FREECAD ASSEMBLY — COMPONENT RECIPES ("cargotrailer_assembly")

This assembly document has 35 components, labeled P0..P34 below (a component is one placed body or linked part). 13 of them carry a construction recipe — the FreeCAD feature program that regenerates the part from scratch, quoted from this document or its linked companion documents; the rest are supplied as boundary geometry only. No exploded tour is included for this assembly.
COMPONENT P0 — recipe-attached ("framefront", a linked part whose construction recipe lives in a companion FreeCAD document of the same project; that document's serialized recipe follows).
Construction recipe (the companion document, serialized — sketch geometry with constraints, then the solid features built on it; lengths are millimeters unless a unit is written):

FCSTD DOCUMENT  (FreeCAD 0.20R29177 (Git))
Label: rightcornersupport
License: All rights reserved
LicenseURL: http://en.wikipedia.org/wiki/All_rights_reserved
objects: Sketcher::SketchObject×4, PartDesign::Pad×2, PartDesign::Pocket×2, PartDesign::LinearPattern×2, PartDesign::MultiTransform×1, PartDesign::Body×1
note: 16 computed .brp shape members not serialized (recipe doc carries the construction recipe); baked Part::Feature solids carry a one-line shape summary decoded from their .brp

FEATURE [Sketcher::SketchObject] Sketch
  FullyConstrained = true
  MapMode = 5
  Placement = pos=(0,0,0) rot=(1,0,0;1.5708rad)
  Support = -> [XZ_Plane]
  sketch-geometry (4):
    g0: LineSegment StartX=0 StartY=0 StartZ=0 EndX=45 EndY=0 EndZ=0
    g1: LineSegment StartX=45 StartY=0 StartZ=0 EndX=45 EndY=42 EndZ=0
    g2: LineSegment StartX=45 StartY=42 StartZ=0 EndX=0 EndY=42 EndZ=0
    g3: LineSegment StartX=0 StartY=42 StartZ=0 EndX=0 EndY=0 EndZ=0
  constraints (11):
    c: Coincident(g0,g1)
    c: Coincident(g1,g2)
    c: Coincident(g2,g3)
    c: Coincident(g3,g0)
    c: Horizontal(g0)
    c: Horizontal(g2)
    c: Vertical(g1)
    c: Vertical(g3)
    c: Coincident(g0,g-1)
    c: DistanceY(g1,g1) = 42
    c: DistanceX(g0,g0) = 45
FEATURE [PartDesign::Pad] Pad
  Direction = (1,1,1)
  Length = 1.6
  Length2 = 100
  Placement = pos=(0,0,0) rot=(1,0,0;1.5708rad)
  Profile = -> Sketch
  Type = 0
FEATURE [Sketcher::SketchObject] Sketch001
  ExternalGeometry = -> [Pad]
  FullyConstrained = true
  MapMode = 5
  Placement = pos=(0,0,0) rot=(-1,0,0;1.5708rad)
  Support = -> [Pad]
  sketch-geometry (4):
    g0: LineSegment StartX=0 StartY=0 StartZ=0 EndX=45 EndY=0 EndZ=0
    g1: LineSegment StartX=45 StartY=0 StartZ=0 EndX=45 EndY=-1.6 EndZ=0
    g2: LineSegment StartX=45 StartY=-1.6 StartZ=0 EndX=0 EndY=-1.6 EndZ=0
    g3: LineSegment StartX=0 StartY=-1.6 StartZ=0 EndX=0 EndY=0 EndZ=0
  constraints (11):
    c: Coincident(g0,g1)
    c: Coincident(g1,g2)
    c: Coincident(g2,g3)
    c: Coincident(g3,g0)
    c: Horizontal(g0)
    c: Horizontal(g2)
    c: Vertical(g1)
    c: Vertical(g3)
    c: Coincident(g0,g-1)
    c: PointOnObject(g1,g-3)
    c: DistanceY(g1,g1) = 1.6
FEATURE [PartDesign::Pad] Pad001
  BaseFeature = -> Pad
  Direction = (1,1,1)
  Length = 31
  Length2 = 100
  Placement = pos=(0,0,0) rot=(1,0,0;1.5708rad)
  Profile = -> Sketch001
  Type = 0
FEATURE [Sketcher::SketchObject] Sketch002
  ExternalGeometry = -> [Pad001]
  FullyConstrained = true
  MapMode = 5
  Placement = pos=(0,-1.6,7e-16) rot=(1,0,0;1.5708rad)
  Support = -> [Pad001]
  sketch-geometry (1):
    g0: Circle CenterX=22.5 CenterY=23.75 CenterZ=0 NormalX=0 NormalY=0 NormalZ=1 AngleXU=0 Radius=7.25
  constraints (3):
    c: Radius(g0) = 7.25
    c: DistanceY(g-1,g0) = 23.75
    c: DistanceX(g-1,g0) = 22.5
FEATURE [PartDesign::Pocket] Pocket
  BaseFeature = -> Pad001
  Direction = (1,1,1)
  Length = 5
  Length2 = 100
  Placement = pos=(0,0,0) rot=(1,0,0;1.5708rad)
  Profile = -> Sketch002
  Type = 1
FEATURE [Sketcher::SketchObject] Sketch003
  FullyConstrained = true
  MapMode = 5
  Placement = pos=(0,1.9e-15,1.6) rot=(0,0,1;3.14159rad)
  Support = -> [Pocket]
  expr: Constraints[1] = 3.3 + 3
  expr: Constraints[2] = 8.9 + 3
  sketch-geometry (1):
    g0: Circle CenterX=-6.3 CenterY=-11.9 CenterZ=0 NormalX=0 NormalY=0 NormalZ=1 AngleXU=0 Radius=3
  constraints (3):
    c: Radius(g0) = 3
    c: DistanceX(g0,g-1) = 6.3
    c: DistanceY(g0,g-1) = 11.9
FEATURE [PartDesign::Pocket] Pocket001
  BaseFeature = -> Pocket
  Direction = (1,1,1)
  Length = 5
  Length2 = 100
  Placement = pos=(0,0,0) rot=(1,0,0;1.5708rad)
  Profile = -> Sketch003
  Type = 1
FEATURE [PartDesign::LinearPattern] LinearPattern
  Direction = -> Y_Axis
  Length = 9.6
  Occurrences = 2
  Placement = pos=(0,0,0) rot=(1,0,0;1.5708rad)
  expr: Length = 3.6 + 6
FEATURE [PartDesign::LinearPattern] LinearPattern001
  Direction = -> X_Axis
  Length = 31
  Occurrences = 2
  Placement = pos=(0,0,0) rot=(1,0,0;1.5708rad)
  expr: Length = 25 + 6
FEATURE [PartDesign::MultiTransform] MultiTransform
  BaseFeature = -> Pocket001
  Originals = -> [Pocket001]
  Placement = pos=(0,0,0) rot=(1,0,0;1.5708rad)
  Transformations = -> [LinearPattern,LinearPattern001]
FEATURE [PartDesign::Body] Body  label="rightcornersupport"
  Group = -> [Sketch,Pad,Sketch001,Pad001,Sketch002,Pocket,Sketch003,Pocket001,MultiTransform,LinearPattern,LinearPattern001]
  Origin = -> Origin
  Tip = -> MultiTransform
COMPONENT P1 — same part as P0; its construction recipe is shown at P0.
COMPONENT P2 — same part as P0; its construction recipe is shown at P0.
COMPONENT P3 — same part as P0; its construction recipe is shown at P0.
COMPONENT P4 — geometry summary ("framecorner003"; no construction recipe available for this part):
  bounding box: 160.0 x 30.0 x 30.0 mm
  tessellated surface: 12 triangles
  volume: 144000 mm^3 (100% of its bounding box)
  symmetry: 4-fold rotationally symmetric about the z axis; mirror-symmetric across its x mid-plane, y mid-plane, z mid-plane
COMPONENT P5 — geometry summary ("framesideright002"; no construction recipe available for this part):
  bounding box: 460.0 x 30.0 x 30.0 mm
  tessellated surface: 12 triangles
  volume: 414000 mm^3 (100% of its bounding box)
  symmetry: 2-fold rotationally symmetric about the x axis; 2-fold rotationally symmetric about the y axis; 2-fold rotationally symmetric about the z axis; mirror-symmetric across its y mid-plane
COMPONENT P6 — geometry summary ("framerear002"; no construction recipe available for this part):
  bounding box: 300.0 x 30.0 x 30.0 mm
  tessellated surface: 12 triangles
  volume: 270000 mm^3 (100% of its bounding box)
  symmetry: 4-fold rotationally symmetric about the x axis; 2-fold rotationally symmetric about the z axis; mirror-symmetric across its x mid-plane, y mid-plane, z mid-plane
COMPONENT P7 — geometry summary ("framecorner007"; no construction recipe available for this part):
  bounding box: 160.0 x 30.0 x 30.0 mm
  tessellated surface: 12 triangles
  volume: 144000 mm^3 (100% of its bounding box)
  symmetry: 4-fold rotationally symmetric about the z axis; mirror-symmetric across its x mid-plane, y mid-plane, z mid-plane
COMPONENT P8 — same part as P0; its construction recipe is shown at P0.
COMPONENT P9 — geometry summary ("rightcornersupport003"; no construction recipe available for this part):
  bounding box: 45.0 x 42.0 x 32.6 mm
  tessellated surface: 1,460 triangles
  volume: 4811 mm^3 (8% of its bounding box)
COMPONENT P10 — geometry summary ("reflectorfront001"; no construction recipe available for this part):
  bounding box: 60.0 x 60.0 x 27.0 mm
  tessellated surface: 1,180 triangles
  volume: 24653 mm^3 (25% of its bounding box)
  symmetry: revolution-symmetric about the y axis through its bounding-box center
COMPONENT P11 — geometry summary ("reflectorrear001"; no construction recipe available for this part):
  bounding box: 60.0 x 60.0 x 27.0 mm
  tessellated surface: 1,180 triangles
  volume: 24653 mm^3 (25% of its bounding box)
  symmetry: revolution-symmetric about the y axis through its bounding-box center
COMPONENT P12 — same part as P0; its construction recipe is shown at P0.
COMPONENT P13 — geometry summary ("rightcornersupport005"; no construction recipe available for this part):
  bounding box: 45.0 x 42.0 x 32.6 mm
  tessellated surface: 1,460 triangles
  volume: 4811 mm^3 (8% of its bounding box)
COMPONENT P14 — geometry summary ("wheel200mm001"; no construction recipe available for this part):
  bounding box: 200.0 x 199.9 x 32.0 mm
  tessellated surface: 19,400 triangles
  volume: 579336 mm^3 (45% of its bounding box)
  symmetry: mirror-symmetric across its x mid-plane
COMPONENT P15 — geometry summary ("Corner003"; no construction recipe available for this part):
  bounding box: 100.0 x 100.0 x 1.5 mm
  tessellated surface: 1,000 triangles
  volume: 4015 mm^3 (27% of its bounding box)
  symmetry: mirror-symmetric across its y mid-plane
COMPONENT P16 — geometry summary ("Do It Garden Raccord 160x065"; no construction recipe available for this part):
  bounding box: 160.0 x 60.0 x 2.0 mm
  tessellated surface: 4,716 triangles
  volume: 18258 mm^3 (95% of its bounding box)
  symmetry: mirror-symmetric across its z mid-plane
COMPONENT P17 — geometry summary ("Do it Garden Equerre 100x100x017"; no construction recipe available for this part):
  bounding box: 100.0 x 100.0 x 1.5 mm
  tessellated surface: 1,000 triangles
  volume: 4015 mm^3 (27% of its bounding box)
  symmetry: mirror-symmetric across its y mid-plane
COMPONENT P18 — same part as P0; its construction recipe is shown at P0.
COMPONENT P19 — geometry summary ("framecorner009"; no construction recipe available for this part):
  bounding box: 160.0 x 30.0 x 30.0 mm
  tessellated surface: 12 triangles
  volume: 144000 mm^3 (100% of its bounding box)
  symmetry: 4-fold rotationally symmetric about the z axis; mirror-symmetric across its x mid-plane, y mid-plane, z mid-plane
COMPONENT P20 — geometry summary ("Do it Garden Plaque de renfort 48x026"; no construction recipe available for this part):
  bounding box: 48.0 x 15.0 x 2.0 mm
  tessellated surface: 796 triangles
  volume: 1283 mm^3 (89% of its bounding box)
  symmetry: 2-fold rotationally symmetric about the x axis; 2-fold rotationally symmetric about the y axis; 2-fold rotationally symmetric about the z axis; mirror-symmetric across its y mid-plane
COMPONENT P21 — geometry summary ("Do it Garden Equerre 70x36x017"; no construction recipe available for this part):
  bounding box: 70.0 x 52.0 x 1.5 mm
  tessellated surface: 1,212 triangles
  volume: 2367 mm^3 (43% of its bounding box)
COMPONENT P22 — geometry summary ("Do it Garden Equerre 70x36x019"; no construction recipe available for this part):
  bounding box: 70.0 x 52.0 x 1.5 mm
  tessellated surface: 1,212 triangles
  volume: 2367 mm^3 (43% of its bounding box)
COMPONENT P23 — geometry summary ("Do it Garden Equerre 30x30x031"; no construction recipe available for this part):
  bounding box: 31.5 x 31.5 x 30.0 mm
  tessellated surface: 808 triangles
  volume: 2650 mm^3 (9% of its bounding box)
COMPONENT P24 — geometry summary ("Do it Garden Equerre 30x30x033"; no construction recipe available for this part):
  bounding box: 31.5 x 31.5 x 30.0 mm
  tessellated surface: 808 triangles
  volume: 2650 mm^3 (9% of its bounding box)
COMPONENT P25 — same part as P0; its construction recipe is shown at P0.
COMPONENT P26 — same part as P0; its construction recipe is shown at P0.
COMPONENT P27 — same part as P0; its construction recipe is shown at P0.
COMPONENT P28 — same part as P0; its construction recipe is shown at P0.
COMPONENT P29 — geometry summary ("Do it Garden Plaque de renfort 48x029"; no construction recipe available for this part):
  bounding box: 48.0 x 15.0 x 2.0 mm
  tessellated surface: 796 triangles
  volume: 1283 mm^3 (89% of its bounding box)
  symmetry: 2-fold rotationally symmetric about the x axis; 2-fold rotationally symmetric about the y axis; 2-fold rotationally symmetric about the z axis; mirror-symmetric across its y mid-plane
COMPONENT P30 — same part as P0; its construction recipe is shown at P0.
COMPONENT P31 — geometry summary ("Series316 Swivel Castor 75mm"; no construction recipe available for this part):
  bounding box: 105.8 x 97.0 x 45.9 mm
  tessellated surface: 66,826 triangles
  volume: 132293 mm^3 (28% of its bounding box)
COMPONENT P32 — geometry summary ("Ayce Connecteur plat galvanise 2x100x036"; no construction recipe available for this part):
  bounding box: 100.0 x 35.0 x 2.0 mm
  tessellated surface: 2,424 triangles
  volume: 6328 mm^3 (90% of its bounding box)
  symmetry: 2-fold rotationally symmetric about the x axis; 2-fold rotationally symmetric about the y axis; 2-fold rotationally symmetric about the z axis; mirror-symmetric across its x mid-plane, y mid-plane, z mid-plane
COMPONENT P33 — geometry summary ("handlebarsides001"; no construction recipe available for this part):
  bounding box: 400.0 x 30.0 x 30.0 mm
  tessellated surface: 12 triangles
  volume: 360000 mm^3 (100% of its bounding box)
  symmetry: 2-fold rotationally symmetric about the x axis; 2-fold rotationally symmetric about the y axis; 2-fold rotationally symmetric about the z axis; mirror-symmetric across its x mid-plane, z mid-plane
COMPONENT P34 — same part as P0; its construction recipe is shown at P0.
PROVENANCE & LICENSES
A FreeCAD (.FCStd) document from a public repository crawl; recipes are the document's own serialized feature recipes (and, for linked parts, companion documents' recipes).
License: as declared in the source repository (recorded in the dataset sidecar).
